# Revit family: Hager-VOLTA-Surface_mounted-IP30-With_Cover-With_DIN-Hosted-CH-en
name_source: partatom
category: Electrical Equipment
units: mm (PartAtom-declared; Revit-internal decimal feet)

## family parameters
Cut with Voids When Loaded = No
Host = Face
Maintain Annotation Orientation = Yes
Panel Configuration = Two Columns, Circuits Across
Part Type = Panelboard
Room Calculation Point = No
Round Connector Dimension = Use Diameter
Shared = No

## types (10) — shared parameters
BC_MODEL_ID = 1547131
BC_OBJECT_ID = 513471
BC_OBJECT_VERSION = #9
Code hager = ADD-EC000214_EU
EF000003 - Mounting method = Surface mounted
EF000008 - Width = 305 mm  [stored 1.00066 ft]
EF000024 - UV resistant = No
EF000049 - Depth = 96 mm  [stored 0.314961 ft]
EF000116 - RAL-number = 9010
EF001062 - EMC-version = No
EF001134 - DIN-rail = Yes
EF002950 - Width in number of modular spacings = 12
EF005474 - Degree of protection (IP) = IP30
EF006244 - Transparent cover/door = No
EF006306 - With lock = No
EF015777 - Neutral terminal block = No
ETIM class code = EC000214
ETIM class name = Small distribution board
HG000001-Number of columns = 1
HG000002-With door or cover = Yes
HG000003-Range = VOLTA
HG000005-Thickness = 2 mm  [stored 0.00656168 ft]
HG000006-Flush mounted = No
HG000009-Double swing door = No
HG000010-Asymmetric doors = No
HG000012-Door swing angle = 90.00°
HG000013-Door on the left = No
HG000014-Door on the right = Yes
HG000015-Clearance visibility = Yes
HG000016-Door 3D visibility = Yes
HG000017-Distance between poles = 18 mm  [stored 0.0590551 ft]
HG000060-RAL-number = 9010
HG000099-Onfly Template ID = 507532
HGEF002950-Width in number of modular spacings = 12
Manufacturer = Hager
Name = VOLTA-Surface_mounted-IP30-With_Cover-With_DIN-CH
Name BIM&CO = Electricity
Name hager = ADD_Enclosures_EC000214
Uniformat = Low Tension Service & Dist.
Uniformat code = D501001
zero-valued in all types: Default Elevation, EF000218 - Built-in depth, EF000846 - Built-in width, EF001131 - Inner depth, HG000007-Number of empty columns

## per-type parameters (varying)
| type | BC_VARIANT_ID | EF000007 - Colour | EF000040 - Height | EF000118 - With mounting plate | EF000266 - Number of rows | EF000332 - Built-in height | EF001088 - Extension possible | EF004462 - Type of closure | EF009212 - Cover model | EF015776 - Earthing terminal block | EF015941 - Signal passing door | HG000004-Manufacturer reference | HG000008-Number of empty rows | HG000011-Empty rows from bottom | HGEF000266-Number of rows |
| VOLTA-Surface_mounted_W305_H245_D96_12_Modular_Spacing-VA12A | 1174202 |  | 245 mm  [stored 0.803806 ft] | No | 1 | 0 mm  [stored 0 ft] | No |  |  | No | No | VA12A | 0 | No | 1 |
| VOLTA-Surface_mounted_W305_H370_D96_12_Modular_Spacing-VA24A | 1174203 | White | 370 mm  [stored 1.21391 ft] | No | 2 | 0 mm  [stored 0 ft] | Yes | Other | With notch | Yes | No | VA24A | 0 | No | 2 |
| VOLTA-Surface_mounted_W305_H515_D96_12_Modular_Spacing-VA36A | 1174204 | White | 515 mm  [stored 1.68963 ft] | No | 3 | 0 mm  [stored 0 ft] | Yes | Other | With notch | Yes | No | VA36A | 0 | No | 3 |
| VOLTA-Surface_mounted_W305_H515_D96_12_Modular_Spacing-VA36RM | 1174207 | White | 515 mm  [stored 1.68963 ft] | No | 3 | 0 mm  [stored 0 ft] | Yes | Other | With notch | No | No | VA36RM | 0 | No | 3 |
| VOLTA-Surface_mounted_W305_H640_D96_12_Modular_Spacing-VA48A | 1174211 | White | 640 mm  [stored 2.09974 ft] | No | 4 | 0 mm  [stored 0 ft] | Yes | Other | With notch | Yes | No | VA48A | 0 | No | 4 |
| VOLTA-Surface_mounted_W305_H765_D96_12_Modular_Spacing-VA602NWS | 1174212 | White | 765 mm  [stored 2.50984 ft] | Yes | 5 | 765 mm  [stored 2.50984 ft] | Yes | Other | With notch | Yes | No | VA602NWS | 3 | Yes | 5 |
| VOLTA-Surface_mounted_W305_H765_D96_12_Modular_Spacing-VA602WWS | 1174213 | White | 765 mm  [stored 2.50984 ft] | Yes | 5 | 765 mm  [stored 2.50984 ft] | Yes | Other | With notch | Yes | Yes | VA602WWS | 3 | Yes | 5 |
| VOLTA-Surface_mounted_W305_H765_D96_12_Modular_Spacing-VA603NWS | 1174214 | White | 765 mm  [stored 2.50984 ft] | Yes | 5 | 765 mm  [stored 2.50984 ft] | Yes | Other | With notch | Yes | No | VA603NWS | 2 | Yes | 5 |
| VOLTA-Surface_mounted_W305_H765_D96_12_Modular_Spacing-VA603WWS | 1174215 | White | 765 mm  [stored 2.50984 ft] | Yes | 5 | 765 mm  [stored 2.50984 ft] | Yes | Other | With notch | Yes | Yes | VA603WWS | 2 | Yes | 5 |
| VOLTA-Surface_mounted_W305_H765_D96_12_Modular_Spacing-VA60A | 1174216 | White | 765 mm  [stored 2.50984 ft] | No | 5 | 0 mm  [stored 0 ft] | Yes | Other | With notch | Yes | No | VA60A | 0 | No | 5 |

note: column(s) folded — value = type name in every type: Reference

note: [stored X ft] marks values corroborated as IEEE doubles in the binary element streams (Revit-internal decimal feet)

## geometry (parser evidence)
native form markers: Sweep x15
no freeform markers — native parametric forms only
